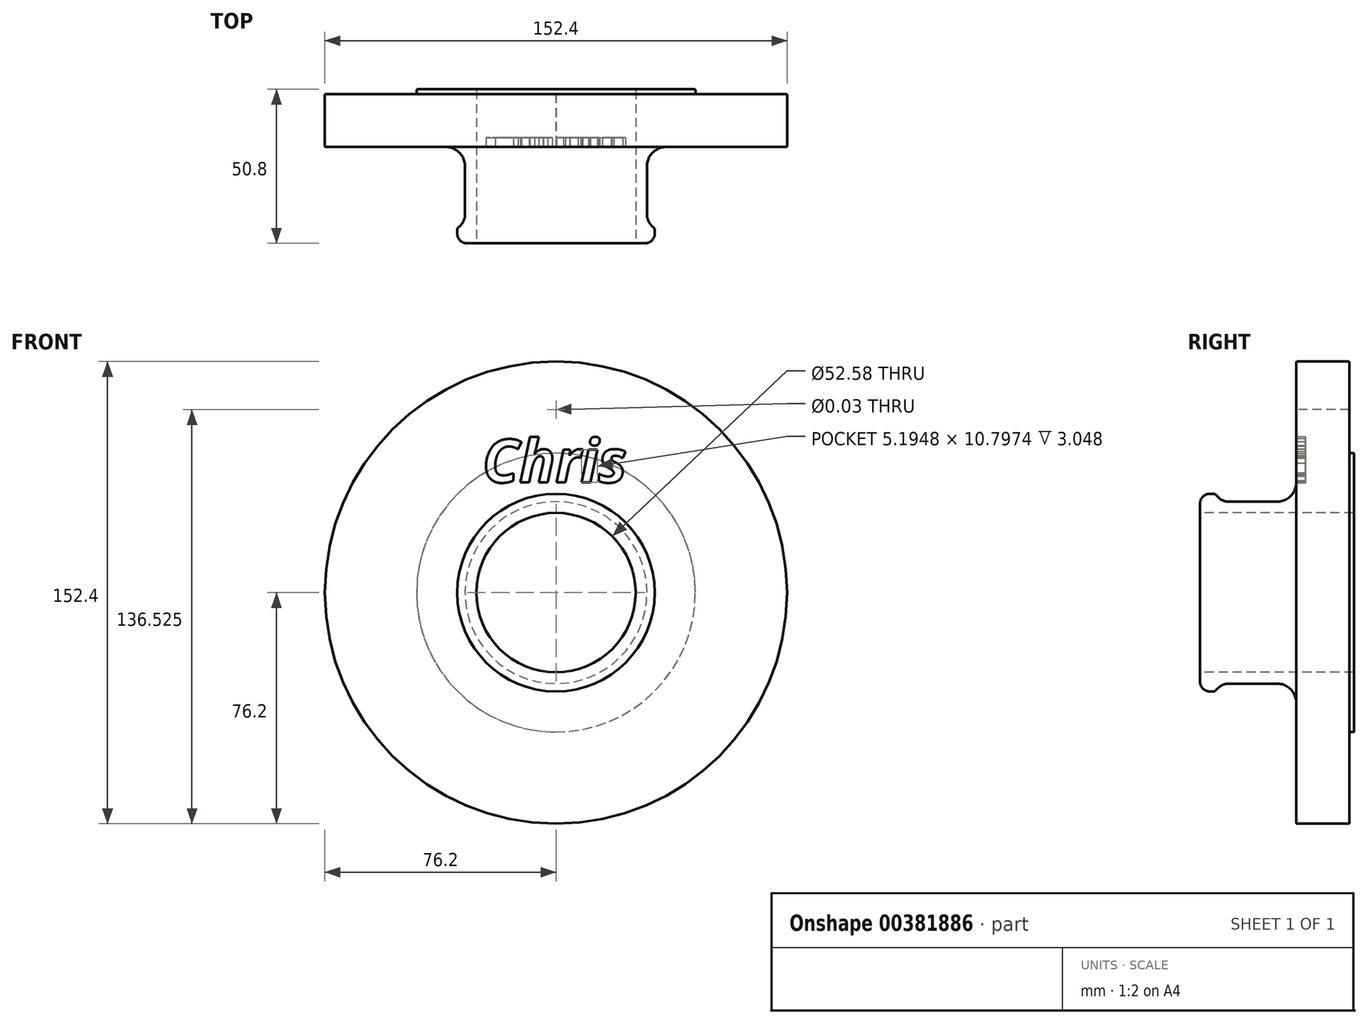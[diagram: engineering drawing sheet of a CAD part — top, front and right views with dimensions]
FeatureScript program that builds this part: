
annotation { "Feature Type Name" : "Feature", "Feature Type Description" : "" }
export const myFeature = defineFeature(function(context is Context, id is Id, definition is map)
    precondition{}
    {
        {
            var Q0;
            Q0=qCreatedBy(makeId("Right.planeOp"),FACE);
            var sketch = newSketch(context, id + "F0", { "sketchPlane" : qUnion([Q0])});
            skLineSegment(sketch, "E0", {"start": v(0, 26.29) * mm, "end": v(0, 29.4) * mm});
            skLineSegment(sketch, "E1", {"start": v(3.17, 32.58) * mm, "end": v(4.4, 32.58) * mm});
            skLineSegment(sketch, "E2", {"start": v(5.1, 32.29) * mm, "end": v(5.9, 31.49) * mm});
            skLineSegment(sketch, "E3", {"start": v(9.5, 30) * mm, "end": v(31.75, 30) * mm});
            skLineSegment(sketch, "E4", {"start": v(31.75, 30) * mm, "end": v(31.75, 76.2) * mm});
            skLineSegment(sketch, "E5", {"start": v(31.75, 76.2) * mm, "end": v(49.23, 76.2) * mm});
            skLineSegment(sketch, "E6", {"start": v(49.23, 76.2) * mm, "end": v(49.23, 45.97) * mm});
            skLineSegment(sketch, "E7", {"start": v(49.23, 45.97) * mm, "end": v(50.8, 45.97) * mm});
            skLineSegment(sketch, "E8", {"start": v(50.8, 45.97) * mm, "end": v(50.8, 26.29) * mm});
            skLineSegment(sketch, "E9", {"start": v(50.8, 26.29) * mm, "end": v(0, 26.29) * mm});
            skLineSegment(sketch, "E10", {"start": v(-25.05, 0) * mm, "end": v(134.12, 0) * mm, "construction": true});
            skPoint(sketch, "E11.visualSharp", {"position": v(0, 32.58) * mm});
            skArc(sketch, "E11.filletArc", {"start": v(3.17, 32.58) * mm, "mid": v(0.93, 31.65) * mm, "end": v(0, 29.4) * mm});
            skPoint(sketch, "E12.visualSharp", {"position": v(4.82, 32.58) * mm});
            skArc(sketch, "E12.filletArc", {"start": v(5.1, 32.29) * mm, "mid": v(4.79, 32.5) * mm, "end": v(4.4, 32.58) * mm});
            skPoint(sketch, "E13.visualSharp", {"position": v(7.4, 30) * mm});
            skArc(sketch, "E13.filletArc", {"start": v(5.9, 31.49) * mm, "mid": v(7.56, 30.38) * mm, "end": v(9.5, 30) * mm});
            skPoint(sketch, "E14.orphan", {"position": v(0, 0) * mm});
            skSolve(sketch);
        }
        {
            var Q0;
            Q0 = qSketchRegion(id + "F0", true);
            var Q1;
            Q1=sQuery(id+"F0.wireOp",EDGE,"E10");
            revolve(context, id + "F1", {"entities" : qUnion([Q0]), "axis" : qUnion([Q1]), "revolveType" : RevolveType.FULL});
        }
        {
            var Q0;
            Q0=makeQuery(id+"F1.opRevolve","SWEPT_EDGE",EDGE,{"disambiguationData":[OSD([sQuery(id+"F0.wireOp",EDGE,"E3"),sQuery(id+"F0.wireOp",EDGE,"E4")])]});
            fillet(context, id + "F2", {"entities" : qUnion([Q0]), "radius" : 6.35 * mm, "tangentPropagation" : true, "allowEdgeOverflow" : false});
        }
        {
            var Q0;
            Q0=makeQuery(id+"F1.opRevolve","SWEPT_FACE",FACE,{"disambiguationData":[OSD([sQuery(id+"F0.wireOp",EDGE,"E4")])]});
            var sketch = newSketch(context, id + "F3", { "sketchPlane" : qUnion([Q0])});
            skPoint(sketch, "E15", {"position": v(0, 60.32) * mm});
            skCircle(sketch, "E16", {"center": v(0, 0) * mm, "radius": 60.32 * mm, "construction": true});
            skSolve(sketch);
        }
        {
            var Q0;
            Q0=sQuery(id+"F3.wireOp",VERTEX,"E15");
            var Q1;
            Q1=makeQuery(id+"F1.opRevolve","SWEPT_BODY",BODY,{"disambiguationData":[OSD([sQuery(id+"F0.wireOp",EDGE,"E0"),sQuery(id+"F0.wireOp",EDGE,"E1"),sQuery(id+"F0.wireOp",EDGE,"E2"),sQuery(id+"F0.wireOp",EDGE,"E3"),sQuery(id+"F0.wireOp",EDGE,"E4"),sQuery(id+"F0.wireOp",EDGE,"E5"),sQuery(id+"F0.wireOp",EDGE,"E6"),sQuery(id+"F0.wireOp",EDGE,"E7"),sQuery(id+"F0.wireOp",EDGE,"E8"),sQuery(id+"F0.wireOp",EDGE,"E9"),sQuery(id+"F0.wireOp",EDGE,"E11.filletArc"),sQuery(id+"F0.wireOp",EDGE,"E12.filletArc"),sQuery(id+"F0.wireOp",EDGE,"E13.filletArc")])]});
            hole(context, id + "F4", {"style" : HoleStyle.SIMPLE, "endStyle" : HoleEndStyle.THROUGH, "standardTappedOrClearance" : lookupTablePath({ "standard" : "ANSI", "size" : "41/64 (0.64)", "type" : "Drilled" }), "standardBlindInLast" : lookupTablePath({ "standard" : "ANSI", "size" : "41/64 (0.64)", "type" : "Drilled" }), "holeDiameter" : 41 / 1625.6 * mm, "majorDiameter" : 6.35 * mm, "isTappedThrough" : true, "tappedDepth" : 12.7 * mm, "tapClearance" : 3, "locations" : qUnion([Q0]), "scope" : qUnion([Q1])});
        }
        {
            var Q0;
            Q0=qCreatedBy(makeId("Right.planeOp"),FACE);
            var sketch = newSketch(context, id + "F5", { "sketchPlane" : qUnion([Q0])});
            skLineSegment(sketch, "E17", {"start": v(0, 0) * mm, "end": v(118.48, 0) * mm, "construction": true});
            skSolve(sketch);
        }
        {
            var Q0;
            Q0=makeQuery(id+"F1.opRevolve","SWEPT_EDGE",EDGE,{"disambiguationData":[OSD([sQuery(id+"F0.wireOp",EDGE,"E4"),sQuery(id+"F0.wireOp",EDGE,"E5")])]});
            var Q1;
            Q1=makeQuery(id+"F1.opRevolve","SWEPT_EDGE",EDGE,{"disambiguationData":[OSD([sQuery(id+"F0.wireOp",EDGE,"E5"),sQuery(id+"F0.wireOp",EDGE,"E6")])]});
            var Q2;
            Q2=makeQuery(id+"F1.opRevolve","SWEPT_EDGE",EDGE,{"disambiguationData":[OSD([sQuery(id+"F0.wireOp",EDGE,"E7"),sQuery(id+"F0.wireOp",EDGE,"E8")])]});
            fillet(context, id + "F6", {"entities" : qUnion([Q0, Q1, Q2]), "radius" : 0.25 * mm, "tangentPropagation" : true, "allowEdgeOverflow" : false});
        }
        {
            var Q0;
            Q0=makeQuery(id+"F1.opRevolve","SWEPT_EDGE",EDGE,{"disambiguationData":[OSD([sQuery(id+"F0.wireOp",EDGE,"E0"),sQuery(id+"F0.wireOp",EDGE,"E9")])]});
            var Q1;
            Q1=makeQuery(id+"F1.opRevolve","SWEPT_EDGE",EDGE,{"disambiguationData":[OSD([sQuery(id+"F0.wireOp",EDGE,"E8"),sQuery(id+"F0.wireOp",EDGE,"E9")])]});
            fillet(context, id + "F7", {"entities" : qUnion([Q0, Q1]), "radius" : 0.25 * mm, "tangentPropagation" : true, "allowEdgeOverflow" : false});
        }
        {
            var Q0;
            Q0=makeQuery(id+"F1.opRevolve","SWEPT_FACE",FACE,{"disambiguationData":[OSD([sQuery(id+"F0.wireOp",EDGE,"E4")])]});
            var sketch = newSketch(context, id + "F8", { "sketchPlane" : qUnion([Q0])});
            skText(sketch, "E18", { "text": "Chris", "fontName": "OpenSans-BoldItalic.ttf"});
            const initialGuessF8  = {"E18": [-0.02425, 0.03635, 1, 0, 0.01424]};
            skSetInitialGuess(sketch, initialGuessF8);
            skSolve(sketch);
        }
        {
            var Q0;
            Q0 = qSketchRegion(id + "F8", true);
            extrude(context, id + "F9", {"entities" : qUnion([Q0]), "operationType" : NewBodyOperationType.REMOVE, "oppositeDirection" : true, "depth" : 3.05 * mm});
        }
    });
